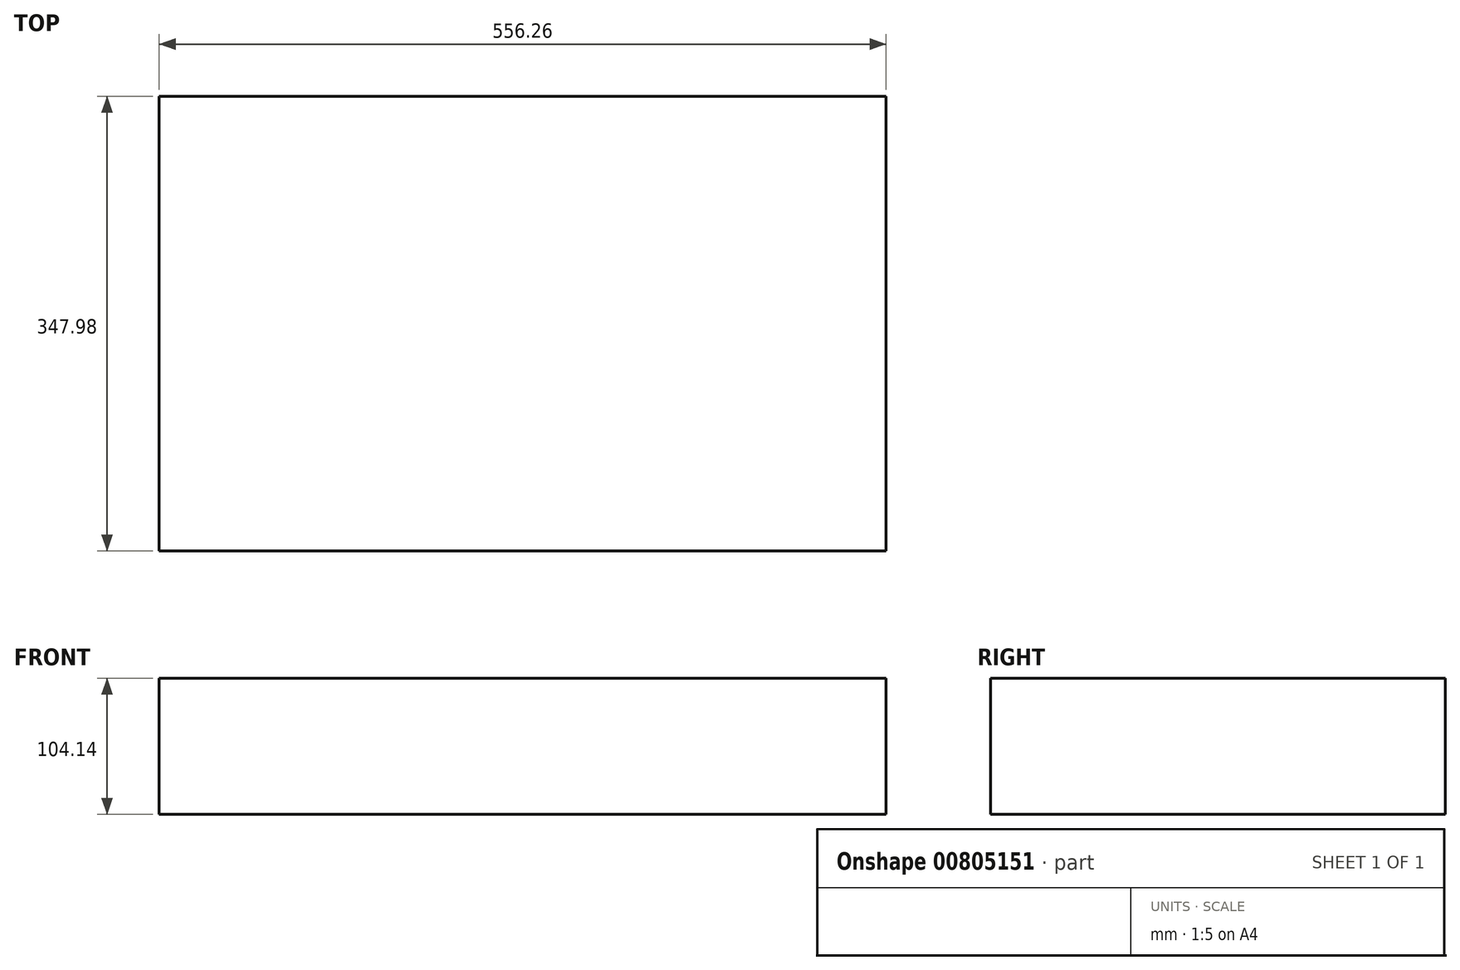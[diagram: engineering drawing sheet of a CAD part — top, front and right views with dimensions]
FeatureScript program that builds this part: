
annotation { "Feature Type Name" : "Feature", "Feature Type Description" : "" }
export const myFeature = defineFeature(function(context is Context, id is Id, definition is map)
    precondition{}
    {
        {
            var Q0;
            Q0=qCreatedBy(makeId("Top.planeOp"),FACE);
            var sketch = newSketch(context, id + "F0", { "sketchPlane" : qUnion([Q0])});
            skLineSegment(sketch, "E0.bottom", {"start": v(-284.58, 91.27) * mm, "end": v(271.68, 91.27) * mm});
            skLineSegment(sketch, "E0.top", {"start": v(-284.58, -256.7) * mm, "end": v(271.68, -256.7) * mm});
            skLineSegment(sketch, "E0.left", {"start": v(-284.58, 91.27) * mm, "end": v(-284.58, -256.7) * mm});
            skLineSegment(sketch, "E0.right", {"start": v(271.68, 91.27) * mm, "end": v(271.68, -256.7) * mm});
            skSolve(sketch);
        }
        {
            var Q0;
            Q0 = qSketchRegion(id + "F0", true);
            extrude(context, id + "F1", {"entities" : qUnion([Q0]), "depth" : 104.14 * mm, "offsetDistance" : 25.4 * mm});
        }
    });
